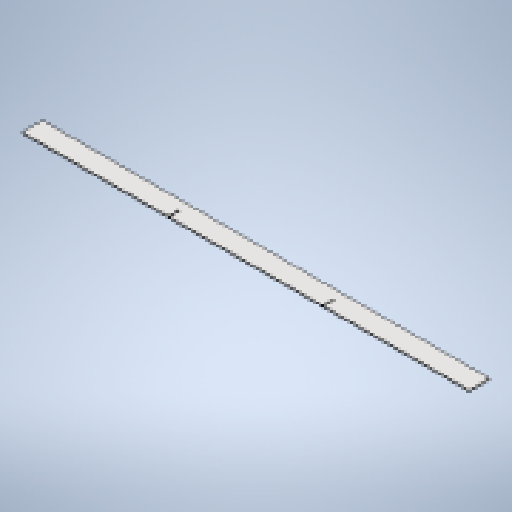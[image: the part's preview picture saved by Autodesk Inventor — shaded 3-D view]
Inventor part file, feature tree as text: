
AUTODESK INVENTOR PART (.ipt)
format: ipt  version: 2025 (Build 290162010, 162A)  size: 221,696 bytes
history: native  units: mm
features: sketch x3, extrude x2, sheet_metal_op x1, other x1, projected_geometry x1
ambient origin geometry x8: Origin, YZ Plane, XZ Plane, XY Plane, X Axis, Y Axis, Z Axis, Center Point
bodies: Body1 (feature_tree)
feature tree (8):
  sheet_metal_op  "Face1"
  extrude  "Extrusion2"  Depth=50.0mm
  extrude  "Extrusion3"  Depth=50.0mm
  sketch  "Sketch1"  dims[d18=50.0mm d19=1200.0mm]
  other  "Plate2"
  sketch  "Sketch3"  dims[d20=3.0mm d25=50.0mm]
  sketch  "Sketch4"  dims[d26=50.0mm d28=3.0mm d29=26.0mm d30=0.0mm d31=0.0mm d35=190.0mm d36=190.0mm d37=3.0mm d38=26.0mm d39=12.217305mm d40=35.0mm d45=67.0mm d46=67.0mm d47=0.0mm d48=0.0mm]
  projected_geometry  "Projected Loop1"
